# Revit family: VE_Exhaust Unit_F_MEPcontent_ClimaRad_Fan
name_source: partatom
category: Mechanical Equipment
revit_build: Autodesk Revit 2018 (Build: 20170223_1515(x64)
units: mm (PartAtom-declared; Revit-internal decimal feet)

## family parameters
Cut with Voids When Loaded = Yes
Host = Face
OmniClass Number = 23.75.70.21.31
OmniClass Title = Exhaust Terminals
Part Type = Normal
Room Calculation Point = Yes
Round Connector Dimension = Use Radius
Shared = No

## types (3) — shared parameters
Article Description = Exhaust fan
Connection Diameter = 100 mm  [stored 0.328084 ft]
Content Supplier URL = www.MEPcontent.com
Custom = No
Description = Exhaust fan
EMCS Version = 3.0
ETIM Article Class = EC010004
Family Version = 11.14
Height = 122 mm  [stored 0.400262 ft]
IFCExportAs = IfcAirTerminalBoxType
Length = 210 mm
MEPcontent Class = EXHAUST_UNIT
Manufacturer = ClimaRad
Manufacturer URL = http://www.climarad.nl
Maximum Flow = 23.6 L/s
Power = 15 W
Product Line = ClimaRad
Radius = 50 mm  [stored 0.164042 ft]
Revit Version = 2018
URL = www.stabiplan.com
Voltage = 230 V
White = Color RAL 9016
Width = 210 mm
zero-valued in all types: Default Elevation

## per-type parameters (varying)
| type | Manufacturer Art. No. |
| B-Fan | 4510100 |
| K-Fan | 4510200 |
| T-Fan | 4510300 |

note: column(s) folded — value = type name in every type: Article Type, Model

note: [stored X ft] marks values corroborated as IEEE doubles in the binary element streams (Revit-internal decimal feet)

## geometry (parser evidence)
native form markers: Sweep x2
no freeform markers — native parametric forms only
